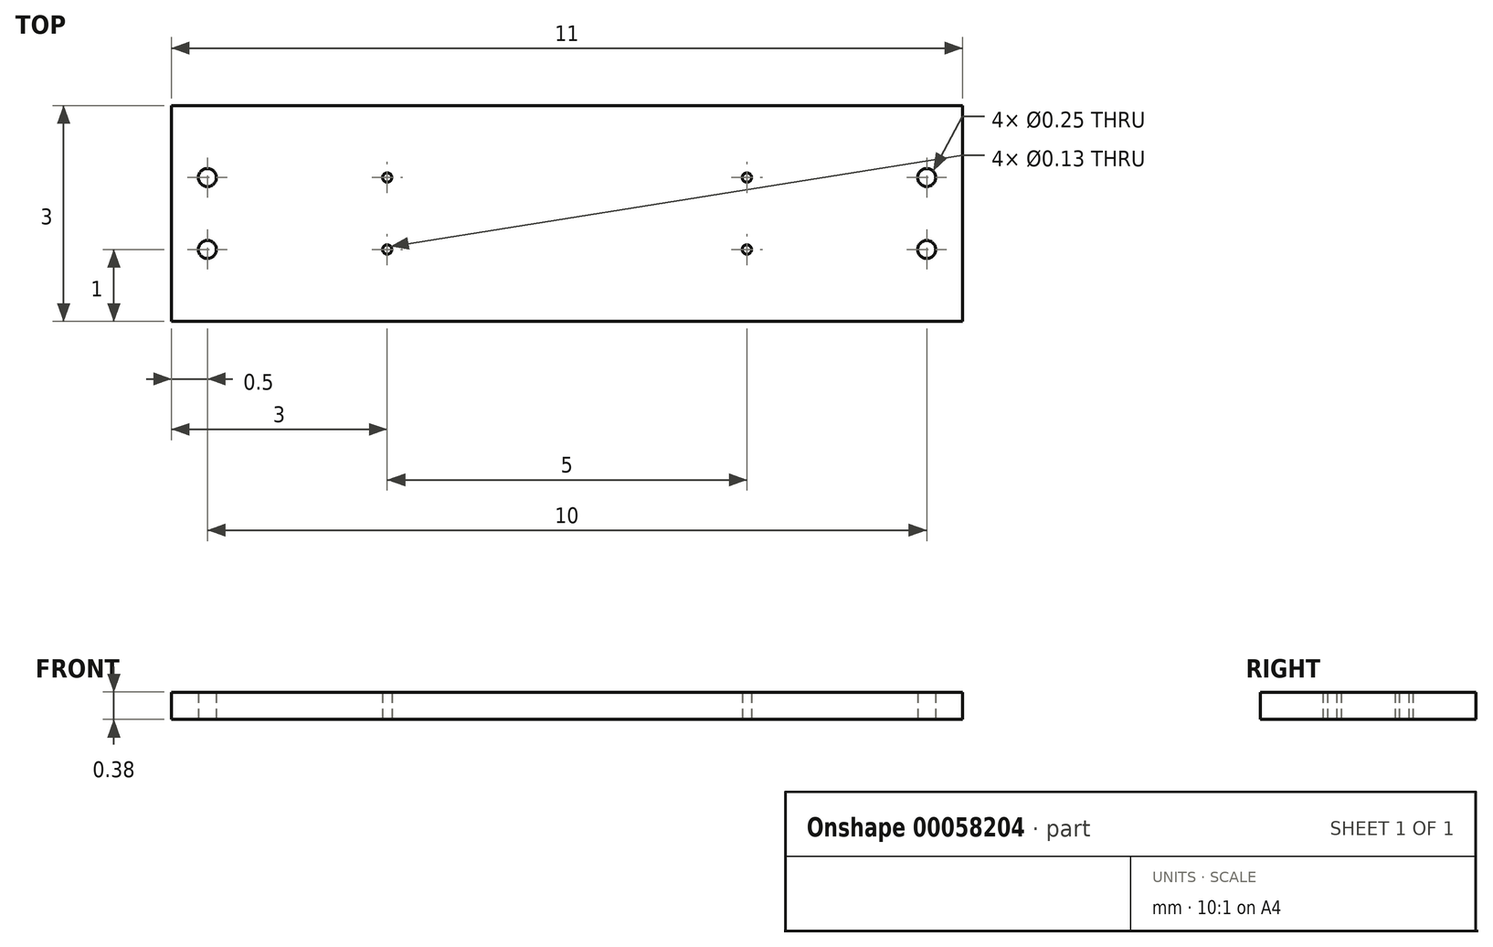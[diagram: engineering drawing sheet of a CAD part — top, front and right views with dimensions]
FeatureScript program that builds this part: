
annotation { "Feature Type Name" : "Feature", "Feature Type Description" : "" }
export const myFeature = defineFeature(function(context is Context, id is Id, definition is map)
    precondition{}
    {
        {
            var Q0;
            Q0=qCreatedBy(makeId("Top.planeOp"),FACE);
            var sketch = newSketch(context, id + "F0", { "sketchPlane" : qUnion([Q0])});
            skLineSegment(sketch, "E0.bottom", {"start": v(-5.5, 1.5) * mm, "end": v(5.5, 1.5) * mm});
            skLineSegment(sketch, "E0.top", {"start": v(-5.5, -1.5) * mm, "end": v(5.5, -1.5) * mm});
            skLineSegment(sketch, "E0.left", {"start": v(-5.5, 1.5) * mm, "end": v(-5.5, -1.5) * mm});
            skLineSegment(sketch, "E0.right", {"start": v(5.5, 1.5) * mm, "end": v(5.5, -1.5) * mm});
            skCircle(sketch, "E1", {"center": v(-5, 0.5) * mm, "radius": 0.12 * mm});
            skCircle(sketch, "E2", {"center": v(-5, -0.5) * mm, "radius": 0.12 * mm});
            skCircle(sketch, "E3", {"center": v(-2.5, 0.5) * mm, "radius": 0.07 * mm});
            skCircle(sketch, "E4", {"center": v(-2.5, -0.5) * mm, "radius": 0.07 * mm});
            skCircle(sketch, "E5", {"center": v(2.5, 0.5) * mm, "radius": 0.07 * mm});
            skCircle(sketch, "E6", {"center": v(2.5, -0.5) * mm, "radius": 0.07 * mm});
            skCircle(sketch, "E7", {"center": v(5, 0.5) * mm, "radius": 0.12 * mm});
            skCircle(sketch, "E8", {"center": v(5, -0.5) * mm, "radius": 0.12 * mm});
            skSolve(sketch);
        }
        {
            var Q0;
            Q0=makeQuery(id+"F0.imprint","IMPRINT",FACE,{"disambiguationData":[TD([[makeQuery(id+"F0.imprint","IMPRINT",EDGE,{"derivedFrom":sQuery(id+"F0.wireOp",EDGE,"E0.bottom")}),-1.0]])]});
            extrude(context, id + "F1", {"entities" : qUnion([Q0]), "endBound" : BoundingType.SYMMETRIC, "depth" : 0.38 * mm});
        }
    });
